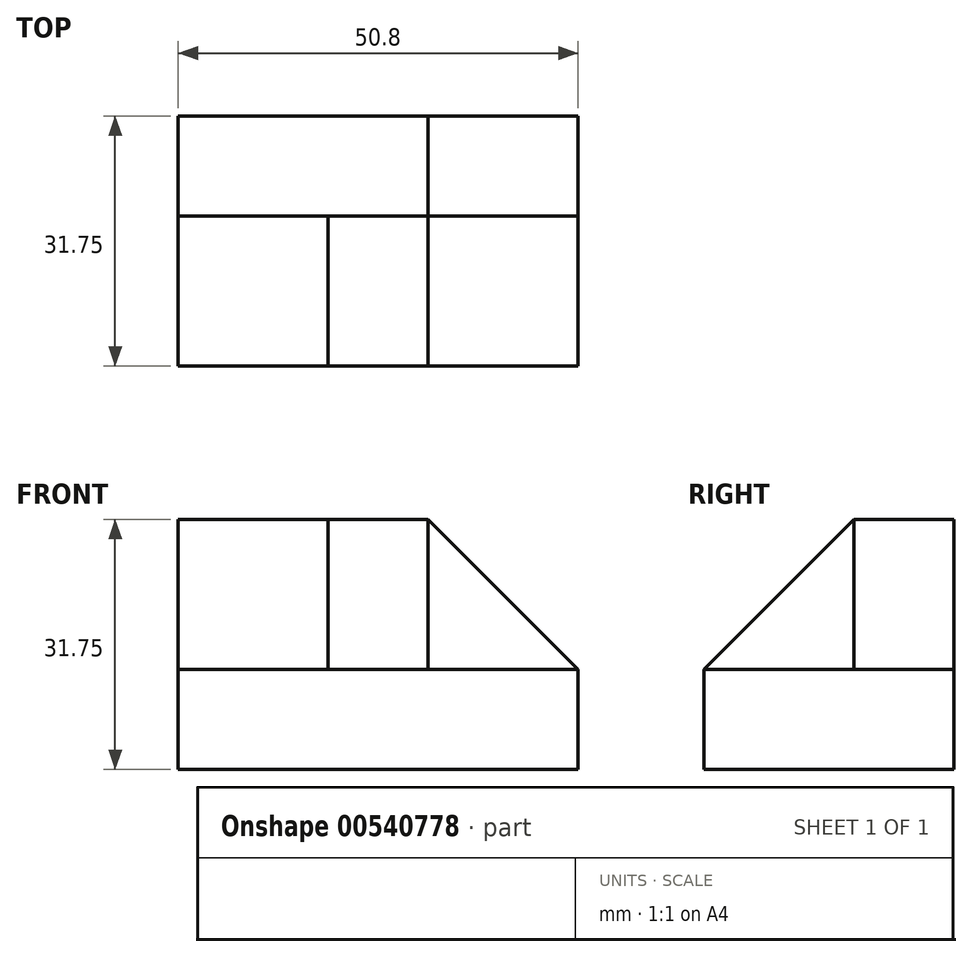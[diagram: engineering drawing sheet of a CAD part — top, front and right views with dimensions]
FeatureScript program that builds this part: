
annotation { "Feature Type Name" : "Feature", "Feature Type Description" : "" }
export const myFeature = defineFeature(function(context is Context, id is Id, definition is map)
    precondition{}
    {
        {
            var Q0;
            Q0=qCreatedBy(makeId("Front.planeOp"),FACE);
            var sketch = newSketch(context, id + "F0", { "sketchPlane" : qUnion([Q0])});
            skLineSegment(sketch, "E0", {"start": v(0, 0) * mm, "end": v(50.8, 0) * mm});
            skLineSegment(sketch, "E1", {"start": v(50.8, 0) * mm, "end": v(50.8, 31.75) * mm});
            skLineSegment(sketch, "E2", {"start": v(50.8, 31.75) * mm, "end": v(0, 31.75) * mm});
            skLineSegment(sketch, "E3", {"start": v(0, 31.75) * mm, "end": v(0, 0) * mm});
            skSolve(sketch);
        }
        {
            var Q0;
            Q0=makeQuery(id+"F0.imprint","IMPRINT",FACE,{"disambiguationData":[TD([[makeQuery(id+"F0.imprint","IMPRINT",EDGE,{"derivedFrom":sQuery(id+"F0.wireOp",EDGE,"E0")}),1.0]])]});
            extrude(context, id + "F1", {"entities" : qUnion([Q0]), "depth" : 31.75 * mm, "offsetDistance" : 25.4 * mm});
        }
        {
            var Q0;
            Q0=makeQuery(id+"F1.opExtrude","CAP_FACE",FACE,{"disambiguationData":[OSD([sQuery(id+"F0.wireOp",EDGE,"E0"),sQuery(id+"F0.wireOp",EDGE,"E1"),sQuery(id+"F0.wireOp",EDGE,"E2"),sQuery(id+"F0.wireOp",EDGE,"E3")])],"isStart":false});
            var sketch = newSketch(context, id + "F2", { "sketchPlane" : qUnion([Q0])});
            skSolve(sketch);
        }
        {
            var Q0;
            Q0=makeQuery(id+"F2.imprint","IMPRINT",FACE,{"disambiguationData":[TD([[makeQuery(id+"F2.imprint","IMPRINT",EDGE,{"derivedFrom":makeQuery(id+"F1.opExtrude","CAP_EDGE",EDGE,{"disambiguationData":[OSD([sQuery(id+"F0.wireOp",EDGE,"E0")])],"isStart":false})}),1.0]])]});
            var sketch = newSketch(context, id + "F3", { "sketchPlane" : qUnion([Q0])});
            skLineSegment(sketch, "E4", {"start": v(19.05, 12.7) * mm, "end": v(0, 12.7) * mm});
            skLineSegment(sketch, "E5", {"start": v(0, 12.7) * mm, "end": v(0, 0) * mm});
            skLineSegment(sketch, "E6", {"start": v(19.05, 12.7) * mm, "end": v(19.05, 31.75) * mm});
            skSolve(sketch);
        }
        {
            var Q0;
            {var subQ0=sQuery(id+"F3.wireOp",EDGE,"E4");Q0=makeQuery(id+"F3.imprint","IMPRINT",FACE,{"disambiguationData":[TD([[makeQuery(id+"F3.imprint","IMPRINT",EDGE,{"derivedFrom":subQ0}),-1.0]])]});}
            extrude(context, id + "F4", {"entities" : qUnion([Q0]), "operationType" : NewBodyOperationType.REMOVE, "oppositeDirection" : true, "depth" : 19.05 * mm, "offsetDistance" : 25.4 * mm});
        }
        {
            var Q0;
            Q0=makeQuery(id+"F2.imprint","IMPRINT",FACE,{"disambiguationData":[TD([[makeQuery(id+"F2.imprint","IMPRINT",EDGE,{"derivedFrom":makeQuery(id+"F1.opExtrude","CAP_EDGE",EDGE,{"disambiguationData":[OSD([sQuery(id+"F0.wireOp",EDGE,"E0")])],"isStart":false})}),1.0]])]});
            var sketch = newSketch(context, id + "F5", { "sketchPlane" : qUnion([Q0])});
            skLineSegment(sketch, "E7", {"start": v(50.8, 0) * mm, "end": v(50.8, 12.7) * mm});
            skLineSegment(sketch, "E8", {"start": v(50.8, 12.7) * mm, "end": v(31.75, 12.7) * mm});
            skLineSegment(sketch, "E9", {"start": v(31.75, 12.7) * mm, "end": v(31.75, 31.75) * mm});
            skSolve(sketch);
        }
        {
            var Q0;
            {var subQ0=sQuery(id+"F5.wireOp",EDGE,"E9");Q0=makeQuery(id+"F5.imprint","IMPRINT",FACE,{"disambiguationData":[TD([[makeQuery(id+"F5.imprint","IMPRINT",EDGE,{"derivedFrom":subQ0}),-1.0]])]});}
            extrude(context, id + "F6", {"entities" : qUnion([Q0]), "operationType" : NewBodyOperationType.REMOVE, "oppositeDirection" : true, "depth" : 19.05 * mm, "offsetDistance" : 25.4 * mm});
        }
        {
            var Q0;
            Q0=makeQuery(id+"F6.boolean.opBoolean","COPY",FACE,{"derivedFrom":makeQuery(id+"F6.opExtrude","SWEPT_FACE",FACE,{"disambiguationData":[OSD([sQuery(id+"F5.wireOp",EDGE,"E9")])]})});
            var sketch = newSketch(context, id + "F7", { "sketchPlane" : qUnion([Q0])});
            skLineSegment(sketch, "E10", {"start": v(-31.75, 12.7) * mm, "end": v(-12.7, 31.75) * mm});
            skSolve(sketch);
        }
        {
            var Q0;
            Q0=makeQuery(id+"F7.imprint","IMPRINT",FACE,{"disambiguationData":[TD([[makeQuery(id+"F7.imprint","IMPRINT",EDGE,{"derivedFrom":sQuery(id+"F7.wireOp",EDGE,"E10")}),1.0]])]});
            extrude(context, id + "F8", {"entities" : qUnion([Q0]), "operationType" : NewBodyOperationType.REMOVE, "oppositeDirection" : true, "depth" : 25.4 * mm, "offsetDistance" : 25.4 * mm});
        }
        {
            var Q0;
            Q0=makeQuery(id+"F6.boolean.opBoolean","COPY",FACE,{"derivedFrom":makeQuery(id+"F6.opExtrude","CAP_FACE",FACE,{"disambiguationData":[OSD([sQuery(id+"F0.wireOp",EDGE,"E1"),sQuery(id+"F0.wireOp",EDGE,"E2"),sQuery(id+"F5.wireOp",EDGE,"E8"),sQuery(id+"F5.wireOp",EDGE,"E9")])],"isStart":false})});
            var sketch = newSketch(context, id + "F9", { "sketchPlane" : qUnion([Q0])});
            skLineSegment(sketch, "E11", {"start": v(31.75, 31.75) * mm, "end": v(50.8, 12.7) * mm});
            skSolve(sketch);
        }
        {
            var Q0;
            Q0=makeQuery(id+"F9.imprint","IMPRINT",FACE,{"disambiguationData":[TD([[makeQuery(id+"F9.imprint","IMPRINT",EDGE,{"derivedFrom":sQuery(id+"F9.wireOp",EDGE,"E11")}),1.0]])]});
            extrude(context, id + "F10", {"entities" : qUnion([Q0]), "operationType" : NewBodyOperationType.REMOVE, "oppositeDirection" : true, "depth" : 25.4 * mm, "offsetDistance" : 25.4 * mm});
        }
    });
